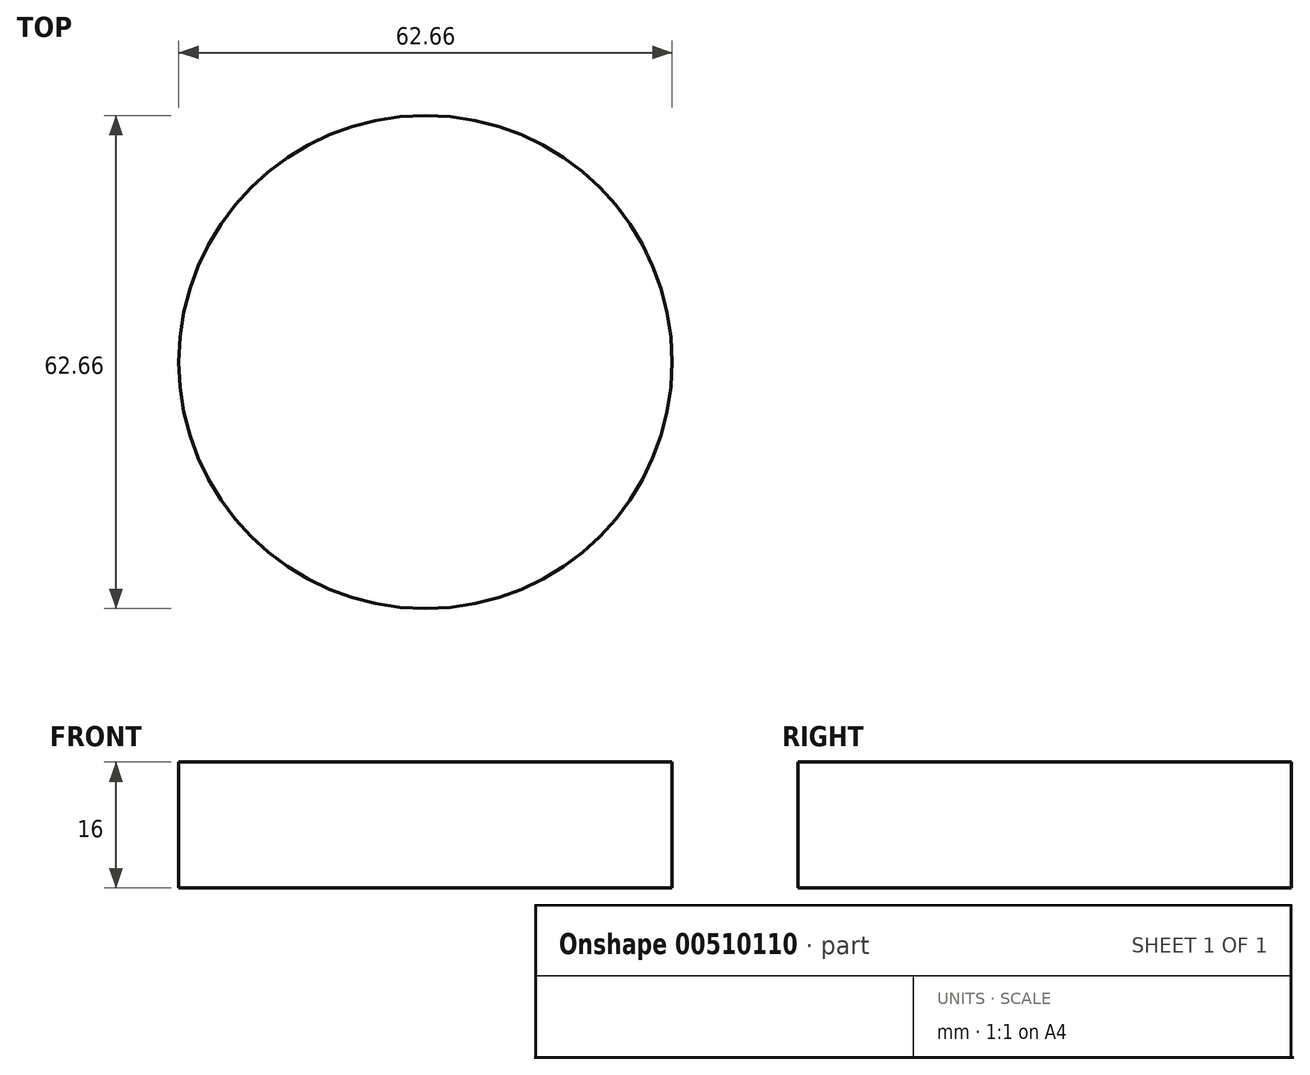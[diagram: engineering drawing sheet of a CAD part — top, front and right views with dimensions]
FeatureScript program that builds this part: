
annotation { "Feature Type Name" : "Feature", "Feature Type Description" : "" }
export const myFeature = defineFeature(function(context is Context, id is Id, definition is map)
    precondition{}
    {
        {
            var Q0;
            Q0=qCreatedBy(makeId("Top.planeOp"),FACE);
            var sketch = newSketch(context, id + "F0", { "sketchPlane" : qUnion([Q0])});
            skCircle(sketch, "E0", {"center": v(0, 0) * mm, "radius": 31.33 * mm});
            skSolve(sketch);
        }
        {
            var Q0;
            Q0=makeQuery(id+"F0.imprint","IMPRINT",FACE,{"disambiguationData":[TD([[makeQuery(id+"F0.imprint","IMPRINT",EDGE,{"derivedFrom":sQuery(id+"F0.wireOp",EDGE,"E0")}),1.0]])]});
            extrude(context, id + "F1", {"entities" : qUnion([Q0]), "depth" : 16 * mm});
        }
    });
